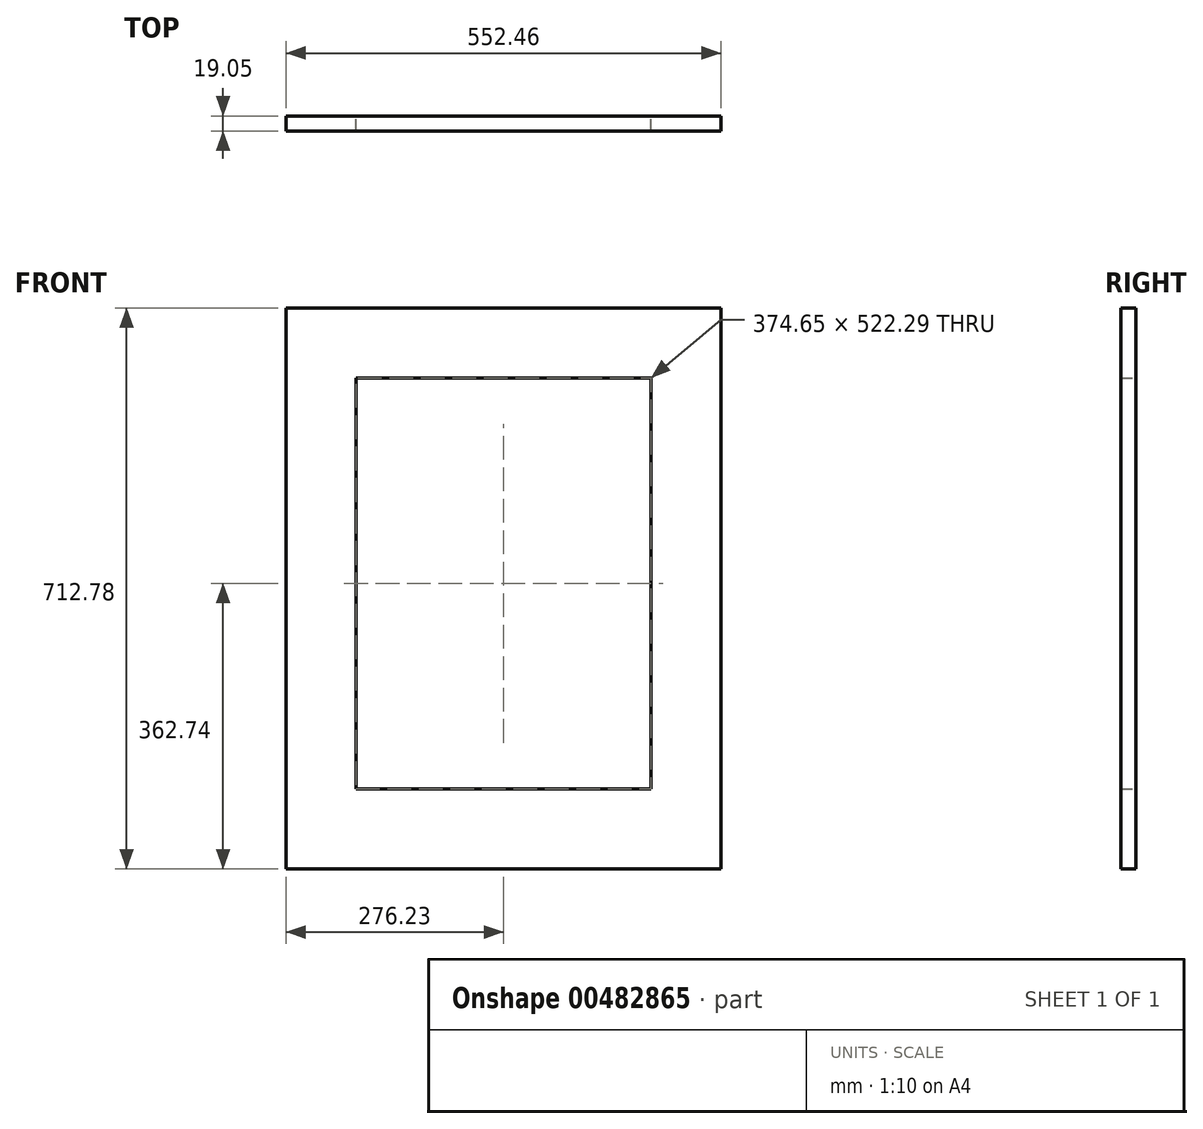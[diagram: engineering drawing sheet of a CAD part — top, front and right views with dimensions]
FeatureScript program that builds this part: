
annotation { "Feature Type Name" : "Feature", "Feature Type Description" : "" }
export const myFeature = defineFeature(function(context is Context, id is Id, definition is map)
    precondition{}
    {
        {
            var Q0;
            Q0=qCreatedBy(makeId("Front.planeOp"),FACE);
            var sketch = newSketch(context, id + "F0", { "sketchPlane" : qUnion([Q0])});
            skLineSegment(sketch, "E0.bottom", {"start": v(276.23, 356.4) * mm, "end": v(-276.23, 356.4) * mm});
            skLineSegment(sketch, "E0.top", {"start": v(276.23, -356.4) * mm, "end": v(-276.23, -356.4) * mm});
            skLineSegment(sketch, "E0.left", {"start": v(276.23, 356.4) * mm, "end": v(276.23, -356.4) * mm});
            skLineSegment(sketch, "E0.right", {"start": v(-276.23, 356.4) * mm, "end": v(-276.23, -356.4) * mm});
            skPoint(sketch, "E0.middle", {"position": v(0, 0) * mm});
            skLineSegment(sketch, "E1.0", {"start": v(187.33, 267.5) * mm, "end": v(-187.32, 267.5) * mm});
            skLineSegment(sketch, "E1.1", {"start": v(187.33, 267.5) * mm, "end": v(187.32, -254.8) * mm});
            skLineSegment(sketch, "E1.3", {"start": v(-187.32, 267.5) * mm, "end": v(-187.33, -254.8) * mm});
            skLineSegment(sketch, "E2", {"start": v(-187.33, -254.8) * mm, "end": v(187.32, -254.8) * mm});
            skSolve(sketch);
        }
        {
            var Q0;
            Q0 = qSketchRegion(id + "F0", true);
            extrude(context, id + "F1", {"entities" : qUnion([Q0]), "depth" : 19.05 * mm});
        }
    });
